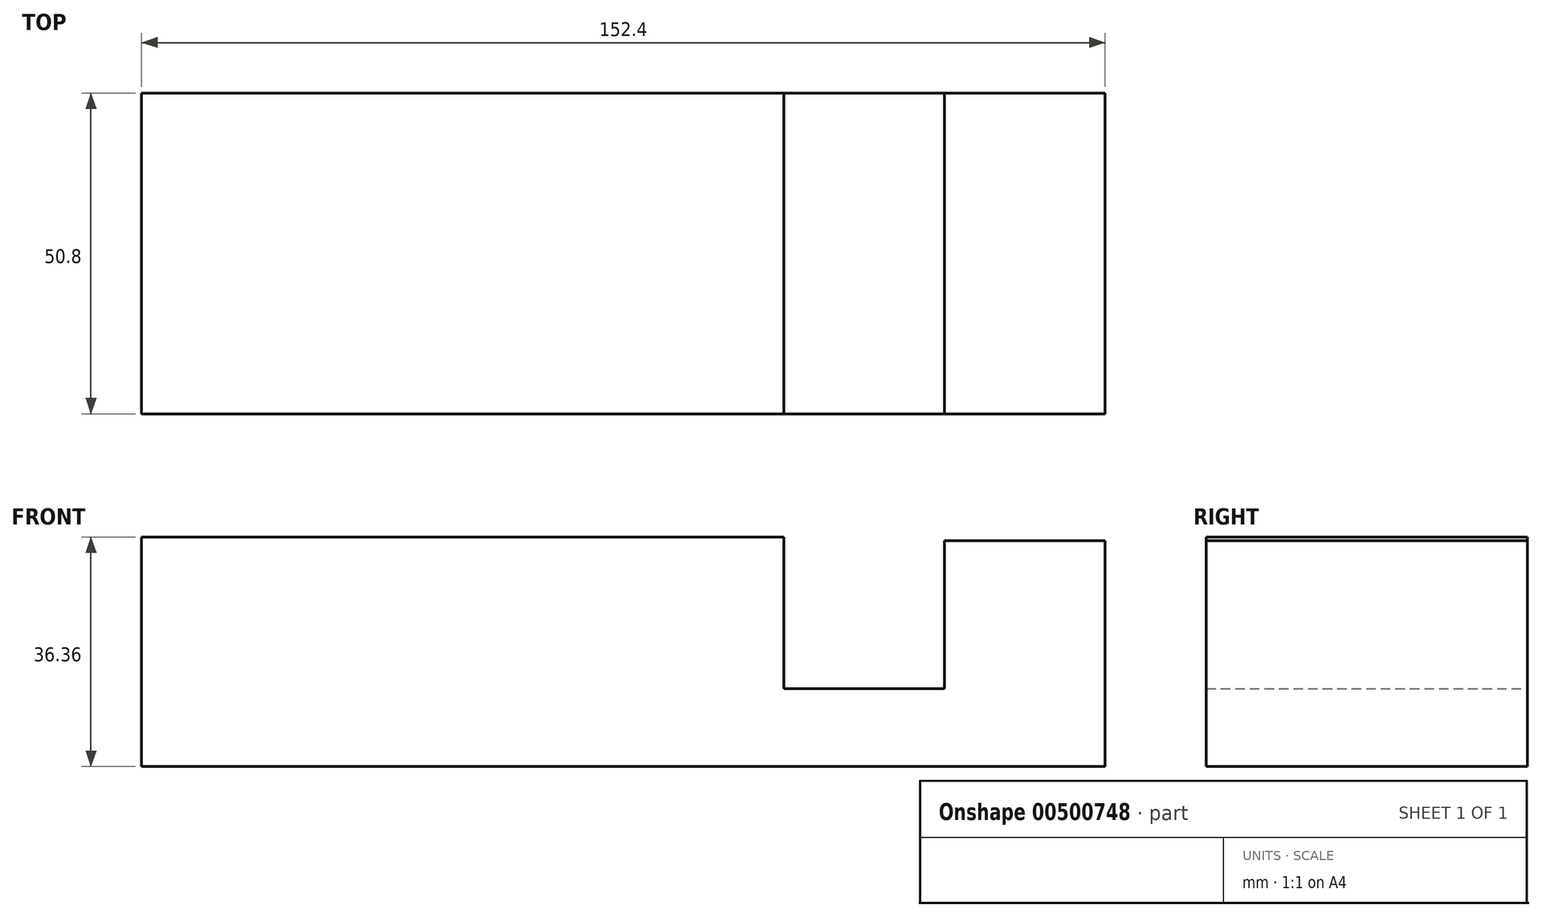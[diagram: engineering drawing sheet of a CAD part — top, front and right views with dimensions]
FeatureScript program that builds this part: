
annotation { "Feature Type Name" : "Feature", "Feature Type Description" : "" }
export const myFeature = defineFeature(function(context is Context, id is Id, definition is map)
    precondition{}
    {
        {
            var Q0;
            Q0=qCreatedBy(makeId("Front.planeOp"),FACE);
            var sketch = newSketch(context, id + "F0", { "sketchPlane" : qUnion([Q0])});
            skLineSegment(sketch, "E0", {"start": v(-134.2, 36.9) * mm, "end": v(-32.6, 36.9) * mm});
            skLineSegment(sketch, "E1", {"start": v(-32.6, 36.9) * mm, "end": v(-32.6, 12.87) * mm});
            skLineSegment(sketch, "E2", {"start": v(-32.6, 12.87) * mm, "end": v(-7.2, 12.87) * mm});
            skLineSegment(sketch, "E3", {"start": v(-7.2, 12.87) * mm, "end": v(-7.2, 36.32) * mm});
            skLineSegment(sketch, "E4", {"start": v(-7.2, 36.32) * mm, "end": v(18.2, 36.32) * mm});
            skLineSegment(sketch, "E5", {"start": v(18.2, 36.32) * mm, "end": v(18.2, 0.54) * mm});
            skLineSegment(sketch, "E6", {"start": v(18.2, 0.54) * mm, "end": v(-134.2, 0.54) * mm});
            skLineSegment(sketch, "E7", {"start": v(-134.2, 0.54) * mm, "end": v(-134.2, 36.9) * mm});
            skSolve(sketch);
        }
        {
            var Q0;
            Q0=makeQuery(id+"F0.imprint","IMPRINT",FACE,{"disambiguationData":[TD([[makeQuery(id+"F0.imprint","IMPRINT",EDGE,{"derivedFrom":sQuery(id+"F0.wireOp",EDGE,"E0")}),-1.0]])]});
            extrude(context, id + "F1", {"entities" : qUnion([Q0]), "depth" : 50.8 * mm});
        }
    });
